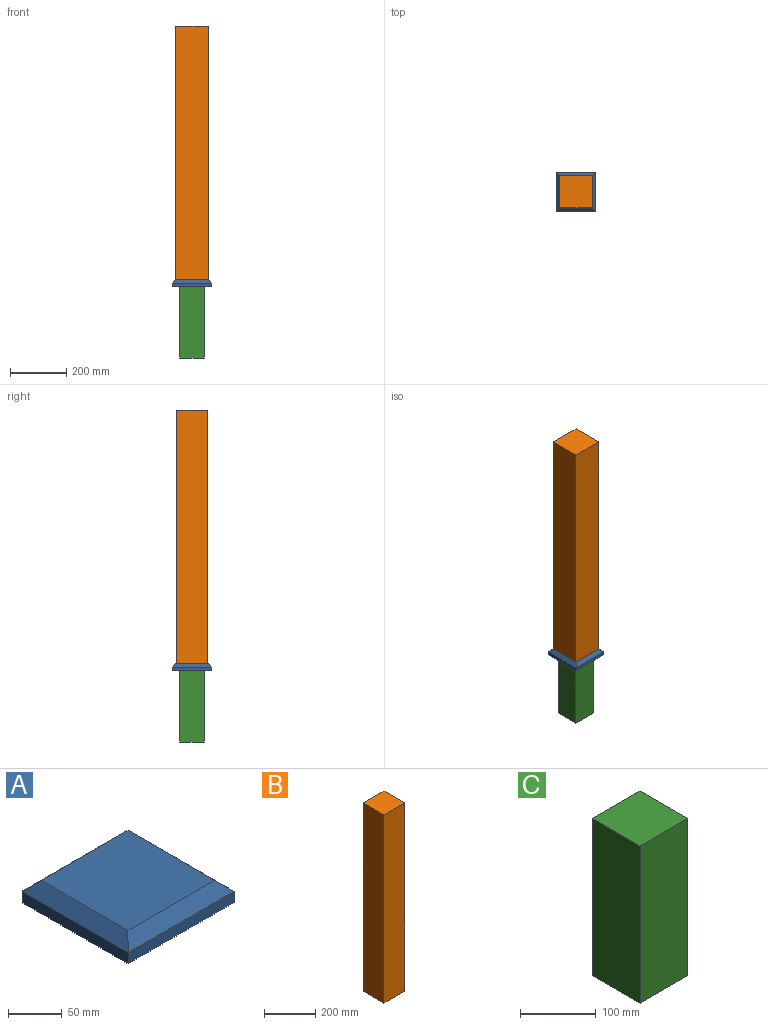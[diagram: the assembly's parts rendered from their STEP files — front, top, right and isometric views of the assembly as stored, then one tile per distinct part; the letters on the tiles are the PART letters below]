
ASSEMBLY  parts=3 mates=2
PART A: 10 faces, bbox 139.7x139.7x25.4 mm
  f0: plane 139.7x12.7mm, normal (0,1,0), area 1774.2mm2, adj f1,f3,f5,f7
  f1: plane 139.7x12.7mm, normal (-1,0,0), area 1774.2mm2, adj f0,f2,f5,f6
  f2: plane 139.7x12.7mm, normal (0,-1,0), area 1774.2mm2, adj f1,f3,f5,f8
  f3: plane 139.7x12.7mm, normal (1,0,0), area 1774.2mm2, adj f0,f2,f5,f9
  f4: plane 114.3x114.3mm, normal (0,0,1), area 13064.5mm2, adj f6,f7,f8,f9
  f5: plane 139.7x139.7mm, normal (0,0,-1), area 19516.1mm2, adj f0,f1,f2,f3
  f6: plane 139.7x12.7mm, normal (-0.71,0,0.71), area 2281mm2, adj f1,f4,f7,f8
  f7: plane 139.7x12.7mm, normal (0,0.71,0.71), area 2281mm2, adj f0,f4,f6,f9
  f8: plane 139.7x12.7mm, normal (0,-0.71,0.71), area 2281mm2, adj f2,f4,f6,f9
  f9: plane 139.7x12.7mm, normal (0.71,0,0.71), area 2281mm2, adj f3,f4,f7,f8
PART B: 6 faces, bbox 114.3x113.7x901.7 mm
  f0: plane 901.7x113.66mm, normal (-1,0,0), area 102485.8mm2, adj f1,f3,f4,f5
  f1: plane 901.7x114.3mm, normal (0,-1,0), area 103064.3mm2, adj f0,f2,f4,f5
  f2: plane 901.7x113.66mm, normal (1,0,0), area 102485.8mm2, adj f1,f3,f4,f5
  f3: plane 901.7x114.3mm, normal (0,1,0), area 103064.3mm2, adj f0,f2,f4,f5
  f4: plane 114.3x113.66mm, normal (0,0,1), area 12991.2mm2, adj f0,f1,f2,f3
  f5: plane 114.3x113.66mm, normal (0,0,-1), area 12991.2mm2, adj f0,f1,f2,f3
PART C: 6 faces, bbox 88.9x88.9x254 mm
  f0: plane 254x88.9mm, normal (0,-1,0), area 22580.6mm2, adj f1,f3,f4,f5
  f1: plane 254x88.9mm, normal (1,0,0), area 22580.6mm2, adj f0,f2,f4,f5
  f2: plane 254x88.9mm, normal (0,1,0), area 22580.6mm2, adj f1,f3,f4,f5
  f3: plane 254x88.9mm, normal (-1,0,0), area 22580.6mm2, adj f0,f2,f4,f5
  f4: plane 88.9x88.9mm, normal (0,0,1), area 7903.2mm2, adj f0,f1,f2,f3
  f5: plane 88.9x88.9mm, normal (0,0,-1), area 7903.2mm2, adj f0,f1,f2,f3
PLACE A t=(-147.87,268.4,-110.82)mm
PLACE B t=(-460.8,113.22,-85.42)mm
PLACE C t=(15.78,95.65,-364.82)mm
MATE fastened C.f4 <-> A.f5  axis (0,0,1) through (-78.02,170.05,-110.82)mm
MATE fastened B.f5 <-> A.f4  axis (0,0,-1) through (-78.02,170.05,-85.42)mm
